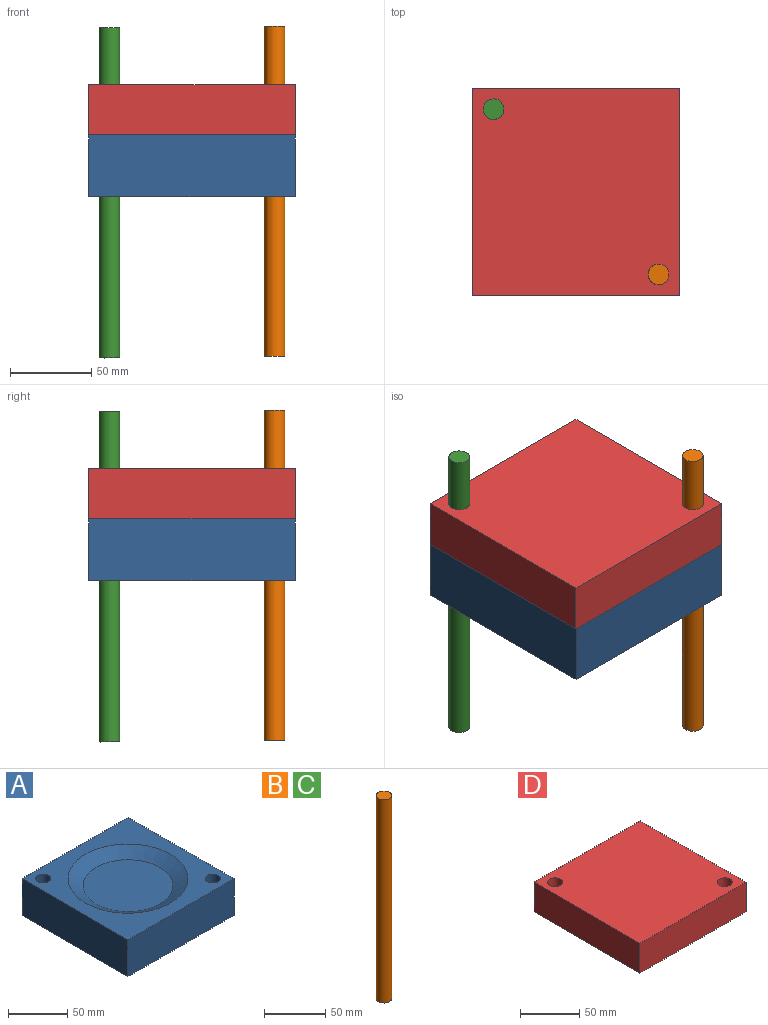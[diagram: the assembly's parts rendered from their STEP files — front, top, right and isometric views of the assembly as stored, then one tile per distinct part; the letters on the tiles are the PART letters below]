
ASSEMBLY  parts=4 mates=4
PART A: 10 faces, bbox 127x127x38.1 mm
  f0: plane 127x127mm, normal (0,0,1), area 7768.3mm2, adj f1,f3,f4,f5,f7,f8,f9
  f1: plane 127x38.1mm, normal (-1,0,0), area 4838.7mm2, adj f0,f2,f4,f5
  f2: plane 127x127mm, normal (0,0,-1), area 15875.6mm2, adj f1,f3,f4,f5,f8,f9
  f3: plane 127x38.1mm, normal (1,0,0), area 4838.7mm2, adj f0,f2,f4,f5
  f4: plane 127x38.1mm, normal (0,-1,0), area 4838.7mm2, adj f0,f1,f2,f3
  f5: plane 127x38.1mm, normal (0,1,0), area 4838.7mm2, adj f0,f1,f2,f3
  f6: plane 76.2x76.2mm, normal (0,0,1), area 4560.4mm2, adj f7
  f7: cone r=50.8mm half-angle=60deg, axis (0,0,1), area 4095.7mm2, adj f0,f6
  f8: cylinder r=6.35mm len=38.1mm, axis (0,0,1), area 1520.1mm2, adj f0,f2
  f9: cylinder r=6.35mm len=38.1mm, axis (0,0,1), area 1520.1mm2, adj f0,f2
PART B: 3 faces, bbox 12.7x12.7x203.2 mm
  f0: cylinder r=6.35mm len=203.2mm, axis (0,0,-1), area 8107.3mm2, adj f1,f2
  f1: plane 12.7x12.7mm, normal (0,0,1), area 126.7mm2, adj f0
  f2: plane 12.7x12.7mm, normal (0,0,-1), area 126.7mm2, adj f0
PART C: same geometry as B
PART D: 10 faces, bbox 127x127x36.6 mm
  f0: plane 127x30.77mm, normal (-1,0,0), area 3907.5mm2, adj f2,f3,f4,f5
  f1: plane 127x30.77mm, normal (1,0,0), area 3907.5mm2, adj f2,f3,f4,f5
  f2: plane 127x30.77mm, normal (0,-1,0), area 3907.5mm2, adj f0,f1,f4,f5
  f3: plane 127x30.77mm, normal (0,1,0), area 3907.5mm2, adj f0,f1,f4,f5
  f4: plane 127x127mm, normal (0,0,1), area 15875.6mm2, adj f0,f1,f2,f3,f8,f9
  f5: plane 127x127mm, normal (0,0,-1), area 8589mm2, adj f0,f1,f2,f3,f6,f8,f9
  f6: cone r=38.1mm half-angle=60deg, axis (0,0,1), area 3148.1mm2, adj f5,f7
  f7: plane 76.2x76.2mm, normal (0,0,-1), area 4560.4mm2, adj f6
  f8: cylinder r=6.35mm len=30.77mm, axis (0,0,1), area 1227.6mm2, adj f4,f5
  f9: cylinder r=6.35mm len=30.77mm, axis (0,0,-1), area 1227.6mm2, adj f4,f5
PLACE A t=(67.12,-27.25,33.9)mm
PLACE B t=(156.92,-92.98,5.12)mm
PLACE C t=(55.32,8.62,4.09)mm
PLACE D t=(67.12,-27.25,32.38)mm
MATE slider C.f0 <-> D.f8  axis (0,0,-1) through (16.32,23.55,4.09)mm
MATE slider A.f8 <-> C.f0  axis (0,0,1) through (16.32,23.55,39.71)mm
MATE slider B.f0 <-> A.f9  axis (0,0,-1) through (117.92,-78.05,5.12)mm
MATE slider B.f0 <-> D.f9  axis (0,0,-1) through (117.92,-78.05,5.12)mm
